# Revit family: DC_Rheem_PLM_HeavyDutyGas_621275
name_source: partatom
category: Plumbing Fixtures
revit_build: Autodesk Revit 2018 (Build: 20170223_1515(x64)
units: mm (PartAtom-declared; Revit-internal decimal feet)

## family parameters
Cut with Voids When Loaded = No
Host = Face
Part Type = Normal
Room Calculation Point = No
Round Connector Dimension = Use Radius
Shared = No

## types (2) — shared parameters
A1_ANZRS = 352 mm
ColdWaterInletHeightH5_ANZRS = 700 mm  [stored 2.29659 ft]
ColdWaterPipeDiameterD4_ANZRS = 32 mm  [stored 0.104987 ft]
ColdWaterPipeRadius_ANZRS = 16 mm  [stored 0.0524934 ft]
CylinderDiameterD3_ANZRS = 643 mm  [stored 2.10958 ft]
CylinderRadius_ANZRS = 322 mm
FireProofBase_ANZRS = 50 mm  [stored 0.164042 ft]
GasInletHeightH4_ANZRS = 340 mm
GasPipeDiameterD2_ANZRS = 20 mm  [stored 0.0656168 ft]
GasPipeRadius_ANZRS = 10 mm  [stored 0.0328084 ft]
HotWaterPipeDiameterD1_ANZRS = 32 mm  [stored 0.104987 ft]
HotWaterPipeHeightH2_ANZRS = 1450 mm
HotWaterPipeRadius_ANZRS = 16 mm  [stored 0.0524934 ft]
Manufacturer = Rheem
Materials_ANZRS = Rheem - Joey Grey Steel
T&PRConnectionRadius_ANZRS = 20 mm  [stored 0.0656168 ft]
ThicknessT_ANZRS = 30 mm
Type Comments = 650L first hour delivery @ 50oC rise
URL = http://www.rheem.com.au
zero-valued in all types: Default Elevation

## per-type parameters (varying)
| type | Description | HeightH3_ANZRS | Model | TotalHeightH1_ANZRS |
| Heavy Duty Gas Storage - Indoor - 275L - 200 MJ/h - Natural gas | Heavy Duty Gas Storage - Indoor - 275L - 110 MJ/h - Natural gas | 1695 mm | 621275N0 | 1895 mm  [stored 6.21719 ft] |
| Heavy Duty Gas Storage - Indoor - 275L - 190/h - Propane gas | Heavy Duty Gas Storage - Indoor - 275L - 100 MJ/h - Propane gas | 1655 mm | 621275P0 | 1795 mm |

note: [stored X ft] marks values corroborated as IEEE doubles in the binary element streams (Revit-internal decimal feet)

## geometry (parser evidence)
native form markers: Blend x6, Sweep x2
no freeform markers — native parametric forms only
